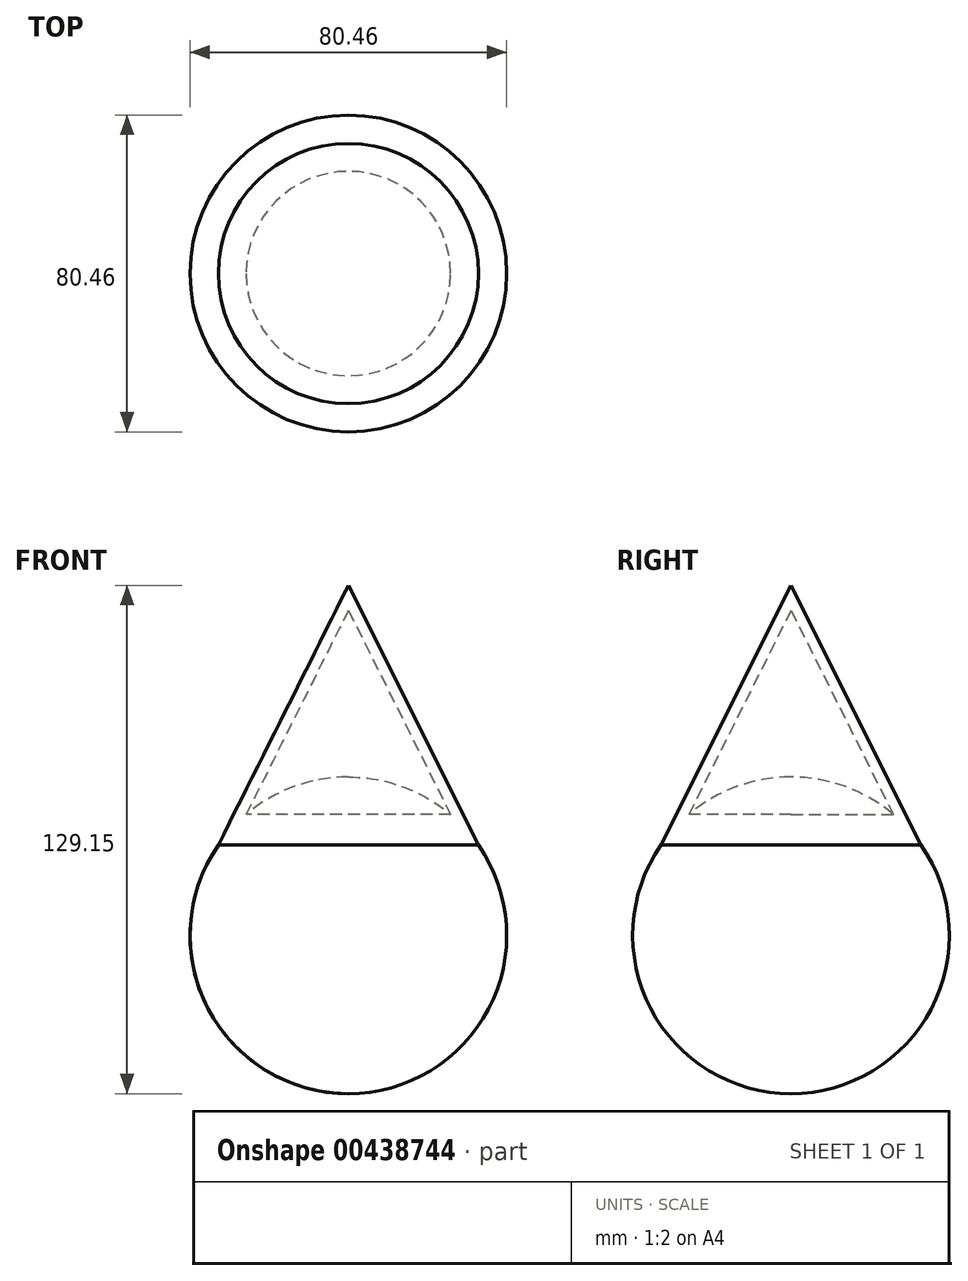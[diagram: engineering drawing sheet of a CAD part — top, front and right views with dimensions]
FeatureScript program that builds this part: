
annotation { "Feature Type Name" : "Feature", "Feature Type Description" : "" }
export const myFeature = defineFeature(function(context is Context, id is Id, definition is map)
    precondition{}
    {
        {
            var Q0;
            Q0=qCreatedBy(makeId("Front.planeOp"),FACE);
            var sketch = newSketch(context, id + "F0", { "sketchPlane" : qUnion([Q0])});
            skLineSegment(sketch, "E0", {"start": v(0, 0) * mm, "end": v(0, 76.2) * mm});
            skLineSegment(sketch, "E1", {"start": v(-38.16, 0) * mm, "end": v(0, 76.2) * mm});
            skLineSegment(sketch, "E2", {"start": v(0, 0) * mm, "end": v(-38.16, 0) * mm});
            skLineSegment(sketch, "E3", {"start": v(0, 0) * mm, "end": v(0, -12.72) * mm});
            skCircle(sketch, "E4", {"center": v(0, -12.72) * mm, "radius": 40.23 * mm});
            skLineSegment(sketch, "E5", {"start": v(0, -15.22) * mm, "end": v(0, -52.95) * mm});
            skLineSegment(sketch, "E6", {"start": v(0, -52.95) * mm, "end": v(0, -12.72) * mm});
            skLineSegment(sketch, "E7", {"start": v(0, 0) * mm, "end": v(0, 69.85) * mm});
            skLineSegment(sketch, "E8", {"start": v(0, 0) * mm, "end": v(-34.98, 0) * mm});
            skLineSegment(sketch, "E9", {"start": v(0, 69.85) * mm, "end": v(-34.98, 0) * mm});
            skSolve(sketch);
        }
        {
            var Q0;
            {var subQ0=sQuery(id+"F0.wireOp",EDGE,"E4");var subQ1=sQuery(id+"F0.wireOp",EDGE,"E1");var subQ3=makeQuery(id+"F0.imprint","INTERSECT",VERTEX,{"derivedFrom":[subQ1,subQ0]});Q0=makeQuery(id+"F0.imprint","IMPRINT",FACE,{"disambiguationData":[TD([[makeQuery(id+"F0.imprint","IMPRINT",EDGE,{"disambiguationData":[TD([[subQ3,1.0]])],"derivedFrom":subQ1}),1.0]])]});}
            var Q1;
            {var subQ0=sQuery(id+"F0.wireOp",EDGE,"E2");Q1=makeQuery(id+"F0.imprint","IMPRINT",FACE,{"disambiguationData":[TD([[makeQuery(id+"F0.imprint","IMPRINT",EDGE,{"derivedFrom":subQ0}),-1.0]])]});}
            var Q2;
            {var subQ0=sQuery(id+"F0.wireOp",EDGE,"E1");var subQ1=sQuery(id+"F0.wireOp",EDGE,"E0");var subQ2=makeQuery(id+"F0.imprint","INTERSECT",VERTEX,{"derivedFrom":[subQ1,subQ0]});Q2=makeQuery(id+"F0.imprint","IMPRINT",FACE,{"disambiguationData":[TD([[makeQuery(id+"F0.imprint","IMPRINT",EDGE,{"disambiguationData":[TD([[subQ2,1.0]])],"derivedFrom":subQ1}),1.0]])]});}
            var Q3;
            {var subQ5=sQuery(id+"F0.wireOp",EDGE,"E2");Q3=makeQuery(id+"F0.imprint","IMPRINT",FACE,{"disambiguationData":[TD([[makeQuery(id+"F0.imprint","IMPRINT",EDGE,{"derivedFrom":subQ5}),1.0]])]});}
            var Q4;
            Q4=sQuery(id+"F0.wireOp",EDGE,"E0");
            revolve(context, id + "F1", {"entities" : qUnion([Q0, Q1, Q2, Q3]), "axis" : qUnion([Q4]), "revolveType" : RevolveType.FULL});
        }
    });
